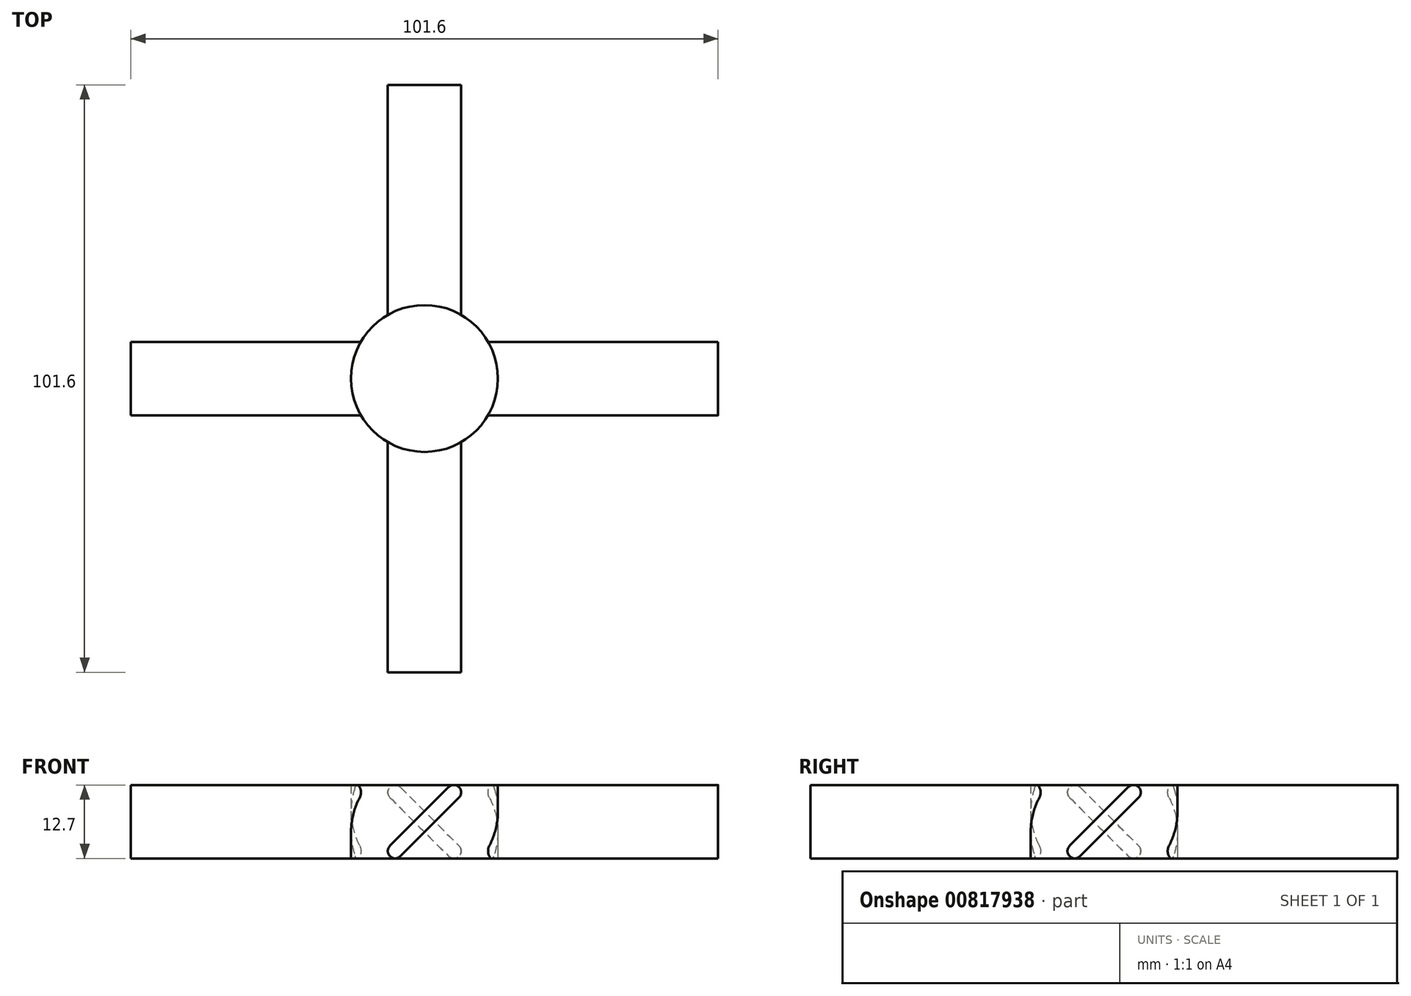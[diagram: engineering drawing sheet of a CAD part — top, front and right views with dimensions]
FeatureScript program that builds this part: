
annotation { "Feature Type Name" : "Feature", "Feature Type Description" : "" }
export const myFeature = defineFeature(function(context is Context, id is Id, definition is map)
    precondition{}
    {
        {
            var Q0;
            Q0=qCreatedBy(makeId("Top.planeOp"),FACE);
            var sketch = newSketch(context, id + "F0", { "sketchPlane" : qUnion([Q0])});
            skCircle(sketch, "E0", {"center": v(0, 0) * mm, "radius": 12.7 * mm});
            skSolve(sketch);
        }
        {
            var Q0;
            Q0 = qSketchRegion(id + "F0", true);
            extrude(context, id + "F1", {"entities" : qUnion([Q0]), "endBound" : BoundingType.SYMMETRIC, "depth" : 12.7 * mm, "offsetDistance" : 25.4 * mm});
        }
        {
            var Q0;
            Q0=qCreatedBy(makeId("Right.planeOp"),FACE);
            var sketch = newSketch(context, id + "F2", { "sketchPlane" : qUnion([Q0])});
            skLineSegment(sketch, "E1.0", {"start": v(-12.7, 6.35) * mm, "end": v(12.7, 6.35) * mm, "construction": true});
            skLineSegment(sketch, "E2.0", {"start": v(-12.7, -6.35) * mm, "end": v(12.7, -6.35) * mm, "construction": true});
            skLineSegment(sketch, "E3", {"start": v(-12.7, -6.35) * mm, "end": v(-12.7, 6.35) * mm, "construction": true});
            skLineSegment(sketch, "E4", {"start": v(12.7, 6.35) * mm, "end": v(12.7, -6.35) * mm, "construction": true});
            skLineSegment(sketch, "E5", {"start": v(6.35, 6.35) * mm, "end": v(-6.35, -6.35) * mm, "construction": true});
            skLineSegment(sketch, "E6.left", {"start": v(5.98, 4.18) * mm, "end": v(-4.18, -5.98) * mm});
            skLineSegment(sketch, "E6.right", {"start": v(4.18, 5.98) * mm, "end": v(-5.98, -4.18) * mm});
            skPoint(sketch, "E6.middle", {"position": v(0, 0) * mm});
            skArc(sketch, "E7", {"start": v(5.98, 4.18) * mm, "mid": v(5.98, 5.98) * mm, "end": v(4.18, 5.98) * mm});
            skArc(sketch, "E8", {"start": v(-5.98, -4.18) * mm, "mid": v(-5.98, -5.98) * mm, "end": v(-4.18, -5.98) * mm});
            skSolve(sketch);
        }
        {
            var Q0;
            Q0 = qSketchRegion(id + "F2", true);
            extrude(context, id + "F3", {"entities" : qUnion([Q0]), "operationType" : NewBodyOperationType.ADD, "depth" : 50.8 * mm, "offsetDistance" : 25.4 * mm});
        }
        {
            var Q0;
            Q0=makeQuery(id+"F1.opExtrude","SWEPT_BODY",BODY,{"disambiguationData":[OSD([sQuery(id+"F0.wireOp",EDGE,"E0")])]});
            var Q1;
            Q1=makeQuery(id+"F1.opExtrude","SWEPT_FACE",FACE,{"disambiguationData":[OSD([sQuery(id+"F0.wireOp",EDGE,"E0")])]});
            circularPattern(context, id + "F4", {"entities" : qUnion([Q0]), "axis" : qUnion([Q1]), "angle" : 360 * degree, "instanceCount" : 4, "equalSpace" : true});
        }
    });
